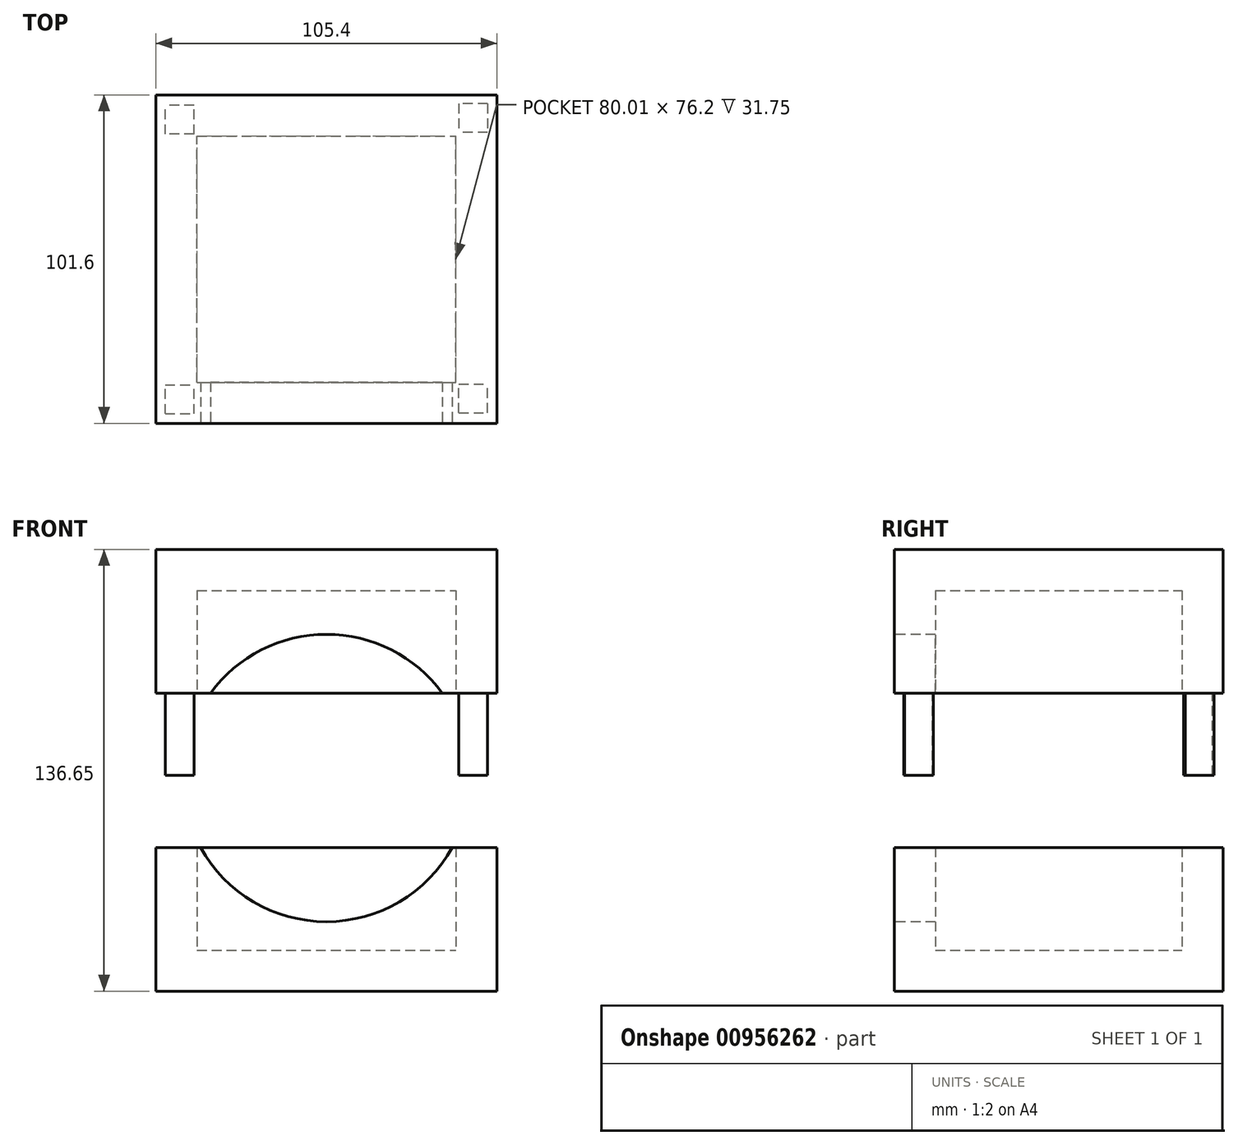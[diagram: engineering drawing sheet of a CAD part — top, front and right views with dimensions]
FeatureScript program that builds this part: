
annotation { "Feature Type Name" : "Feature", "Feature Type Description" : "" }
export const myFeature = defineFeature(function(context is Context, id is Id, definition is map)
    precondition{}
    {
        {
            var Q0;
            Q0=qCreatedBy(makeId("Front.planeOp"),FACE);
            var sketch = newSketch(context, id + "F0", { "sketchPlane" : qUnion([Q0])});
            skLineSegment(sketch, "E0.bottom", {"start": v(-52.7, 70.73) * mm, "end": v(52.7, 70.73) * mm});
            skLineSegment(sketch, "E0.top", {"start": v(-52.7, 26.28) * mm, "end": v(52.7, 26.28) * mm});
            skLineSegment(sketch, "E0.left", {"start": v(-52.7, 70.73) * mm, "end": v(-52.7, 26.28) * mm});
            skLineSegment(sketch, "E0.right", {"start": v(52.7, 70.73) * mm, "end": v(52.7, 26.28) * mm});
            skPoint(sketch, "E0.middle", {"position": v(0, 48.5) * mm});
            skLineSegment(sketch, "E1.bottom", {"start": v(-52.7, -21.47) * mm, "end": v(52.7, -21.47) * mm});
            skLineSegment(sketch, "E1.top", {"start": v(-52.7, -65.92) * mm, "end": v(52.7, -65.92) * mm});
            skLineSegment(sketch, "E1.left", {"start": v(-52.7, -21.47) * mm, "end": v(-52.7, -65.92) * mm});
            skLineSegment(sketch, "E1.right", {"start": v(52.7, -21.47) * mm, "end": v(52.7, -65.92) * mm});
            skPoint(sketch, "E1.middle", {"position": v(0, -43.7) * mm});
            skSolve(sketch);
        }
        {
            var Q0;
            Q0=makeQuery(id+"F0.imprint","IMPRINT",FACE,{"disambiguationData":[TD([[makeQuery(id+"F0.imprint","IMPRINT",EDGE,{"derivedFrom":sQuery(id+"F0.wireOp",EDGE,"E0.bottom")}),-1.0]])]});
            var Q1;
            Q1=makeQuery(id+"F0.imprint","IMPRINT",FACE,{"disambiguationData":[TD([[makeQuery(id+"F0.imprint","IMPRINT",EDGE,{"derivedFrom":sQuery(id+"F0.wireOp",EDGE,"E1.bottom")}),-1.0]])]});
            extrude(context, id + "F1", {"entities" : qUnion([Q0, Q1]), "endBound" : BoundingType.SYMMETRIC, "depth" : 101.6 * mm, "offsetDistance" : 25.4 * mm});
        }
        {
            var Q0;
            Q0=makeQuery(id+"F1.opExtrude","SWEPT_FACE",FACE,{"disambiguationData":[OSD([sQuery(id+"F0.wireOp",EDGE,"E1.bottom")])]});
            var Q1;
            Q1=makeQuery(id+"F1.opExtrude","SWEPT_FACE",FACE,{"disambiguationData":[OSD([sQuery(id+"F0.wireOp",EDGE,"E0.top")])]});
            shell(context, id + "F2", {"entities" : qUnion([Q0, Q1]), "thickness" : 12.7 * mm});
        }
        {
            var Q0;
            Q0=makeQuery(id+"F1.opExtrude","CAP_FACE",FACE,{"disambiguationData":[OSD([sQuery(id+"F0.wireOp",EDGE,"E0.bottom"),sQuery(id+"F0.wireOp",EDGE,"E0.top"),sQuery(id+"F0.wireOp",EDGE,"E0.left"),sQuery(id+"F0.wireOp",EDGE,"E0.right")])],"isStart":false});
            var sketch = newSketch(context, id + "F3", { "sketchPlane" : qUnion([Q0])});
            skCircle(sketch, "E2", {"center": v(0, 0) * mm, "radius": 44.45 * mm});
            skSolve(sketch);
        }
        {
            var Q0;
            {var subQ0=sQuery(id+"F3.wireOp",EDGE,"E2");var subQ1=makeQuery(id+"F1.opExtrude","CAP_EDGE",EDGE,{"disambiguationData":[OSD([sQuery(id+"F0.wireOp",EDGE,"E0.top")])],"isStart":false});var subQ2=makeQuery(id+"F3.imprint","INTERSECT",VERTEX,{"disambiguationData":[OD(0.0)],"derivedFrom":[subQ1,subQ0]});Q0=makeQuery(id+"F3.imprint","IMPRINT",FACE,{"disambiguationData":[TD([[makeQuery(id+"F3.imprint","IMPRINT",EDGE,{"disambiguationData":[TD([[subQ2,1.0]])],"derivedFrom":subQ0}),1.0]])]});}
            extrude(context, id + "F4", {"entities" : qUnion([Q0]), "operationType" : NewBodyOperationType.REMOVE, "oppositeDirection" : true, "depth" : 25.4 * mm, "offsetDistance" : 25.4 * mm});
        }
        {
            var Q0;
            Q0=makeQuery(id+"F1.opExtrude","CAP_FACE",FACE,{"disambiguationData":[OSD([sQuery(id+"F0.wireOp",EDGE,"E1.bottom"),sQuery(id+"F0.wireOp",EDGE,"E1.top"),sQuery(id+"F0.wireOp",EDGE,"E1.left"),sQuery(id+"F0.wireOp",EDGE,"E1.right")])],"isStart":false});
            var sketch = newSketch(context, id + "F5", { "sketchPlane" : qUnion([Q0])});
            skCircle(sketch, "E3", {"center": v(0, 0) * mm, "radius": 44.45 * mm});
            skSolve(sketch);
        }
        {
            var Q0;
            {var subQ0=sQuery(id+"F5.wireOp",EDGE,"E3");var subQ1=makeQuery(id+"F1.opExtrude","CAP_EDGE",EDGE,{"disambiguationData":[OSD([sQuery(id+"F0.wireOp",EDGE,"E1.bottom")])],"isStart":false});var subQ2=makeQuery(id+"F5.imprint","INTERSECT",VERTEX,{"disambiguationData":[OD(0.0)],"derivedFrom":[subQ1,subQ0]});Q0=makeQuery(id+"F5.imprint","IMPRINT",FACE,{"disambiguationData":[TD([[makeQuery(id+"F5.imprint","IMPRINT",EDGE,{"disambiguationData":[TD([[subQ2,-1.0]])],"derivedFrom":subQ0}),1.0]])]});}
            extrude(context, id + "F6", {"entities" : qUnion([Q0]), "operationType" : NewBodyOperationType.REMOVE, "oppositeDirection" : true, "depth" : 25.4 * mm, "offsetDistance" : 25.4 * mm});
        }
        {
            var Q0;
            Q0=makeQuery(id+"F1.opExtrude","SWEPT_FACE",FACE,{"disambiguationData":[OSD([sQuery(id+"F0.wireOp",EDGE,"E0.top")])]});
            var sketch = newSketch(context, id + "F7", { "sketchPlane" : qUnion([Q0])});
            skLineSegment(sketch, "E4.bottom", {"start": v(-49.82, 47.85) * mm, "end": v(-40.93, 47.85) * mm});
            skLineSegment(sketch, "E4.top", {"start": v(-49.82, 38.96) * mm, "end": v(-40.93, 38.96) * mm});
            skLineSegment(sketch, "E4.left", {"start": v(-49.82, 47.85) * mm, "end": v(-49.82, 38.96) * mm});
            skLineSegment(sketch, "E4.right", {"start": v(-40.93, 47.85) * mm, "end": v(-40.93, 38.96) * mm});
            skLineSegment(sketch, "E5.bottom", {"start": v(40.93, 47.55) * mm, "end": v(49.82, 47.55) * mm});
            skLineSegment(sketch, "E5.top", {"start": v(40.93, 38.66) * mm, "end": v(49.82, 38.66) * mm});
            skLineSegment(sketch, "E5.left", {"start": v(40.93, 47.55) * mm, "end": v(40.93, 38.66) * mm});
            skLineSegment(sketch, "E5.right", {"start": v(49.82, 47.55) * mm, "end": v(49.82, 38.66) * mm});
            skLineSegment(sketch, "E6.bottom", {"start": v(-40.92, -38.64) * mm, "end": v(-49.8, -38.64) * mm});
            skLineSegment(sketch, "E6.top", {"start": v(-40.92, -47.53) * mm, "end": v(-49.8, -47.53) * mm});
            skLineSegment(sketch, "E6.left", {"start": v(-40.92, -38.64) * mm, "end": v(-40.92, -47.53) * mm});
            skLineSegment(sketch, "E6.right", {"start": v(-49.8, -38.64) * mm, "end": v(-49.8, -47.53) * mm});
            skLineSegment(sketch, "E7.bottom", {"start": v(49.8, -48.08) * mm, "end": v(40.92, -48.08) * mm});
            skLineSegment(sketch, "E7.top", {"start": v(49.8, -39.19) * mm, "end": v(40.92, -39.19) * mm});
            skLineSegment(sketch, "E7.left", {"start": v(49.8, -48.08) * mm, "end": v(49.8, -39.19) * mm});
            skLineSegment(sketch, "E7.right", {"start": v(40.92, -48.08) * mm, "end": v(40.92, -39.19) * mm});
            skSolve(sketch);
        }
        {
            var Q0;
            Q0=makeQuery(id+"F7.imprint","IMPRINT",FACE,{"disambiguationData":[TD([[makeQuery(id+"F7.imprint","IMPRINT",EDGE,{"derivedFrom":sQuery(id+"F7.wireOp",EDGE,"E4.bottom")}),-1.0]])]});
            var Q1;
            Q1=makeQuery(id+"F7.imprint","IMPRINT",FACE,{"disambiguationData":[TD([[makeQuery(id+"F7.imprint","IMPRINT",EDGE,{"derivedFrom":sQuery(id+"F7.wireOp",EDGE,"E6.bottom")}),1.0]])]});
            var Q2;
            Q2=makeQuery(id+"F7.imprint","IMPRINT",FACE,{"disambiguationData":[TD([[makeQuery(id+"F7.imprint","IMPRINT",EDGE,{"derivedFrom":sQuery(id+"F7.wireOp",EDGE,"E5.bottom")}),-1.0]])]});
            var Q3;
            Q3=makeQuery(id+"F7.imprint","IMPRINT",FACE,{"disambiguationData":[TD([[makeQuery(id+"F7.imprint","IMPRINT",EDGE,{"derivedFrom":sQuery(id+"F7.wireOp",EDGE,"E7.bottom")}),-1.0]])]});
            extrude(context, id + "F8", {"entities" : qUnion([Q0, Q1, Q2, Q3]), "operationType" : NewBodyOperationType.ADD, "depth" : 25.4 * mm, "offsetDistance" : 25.4 * mm});
        }
    });
